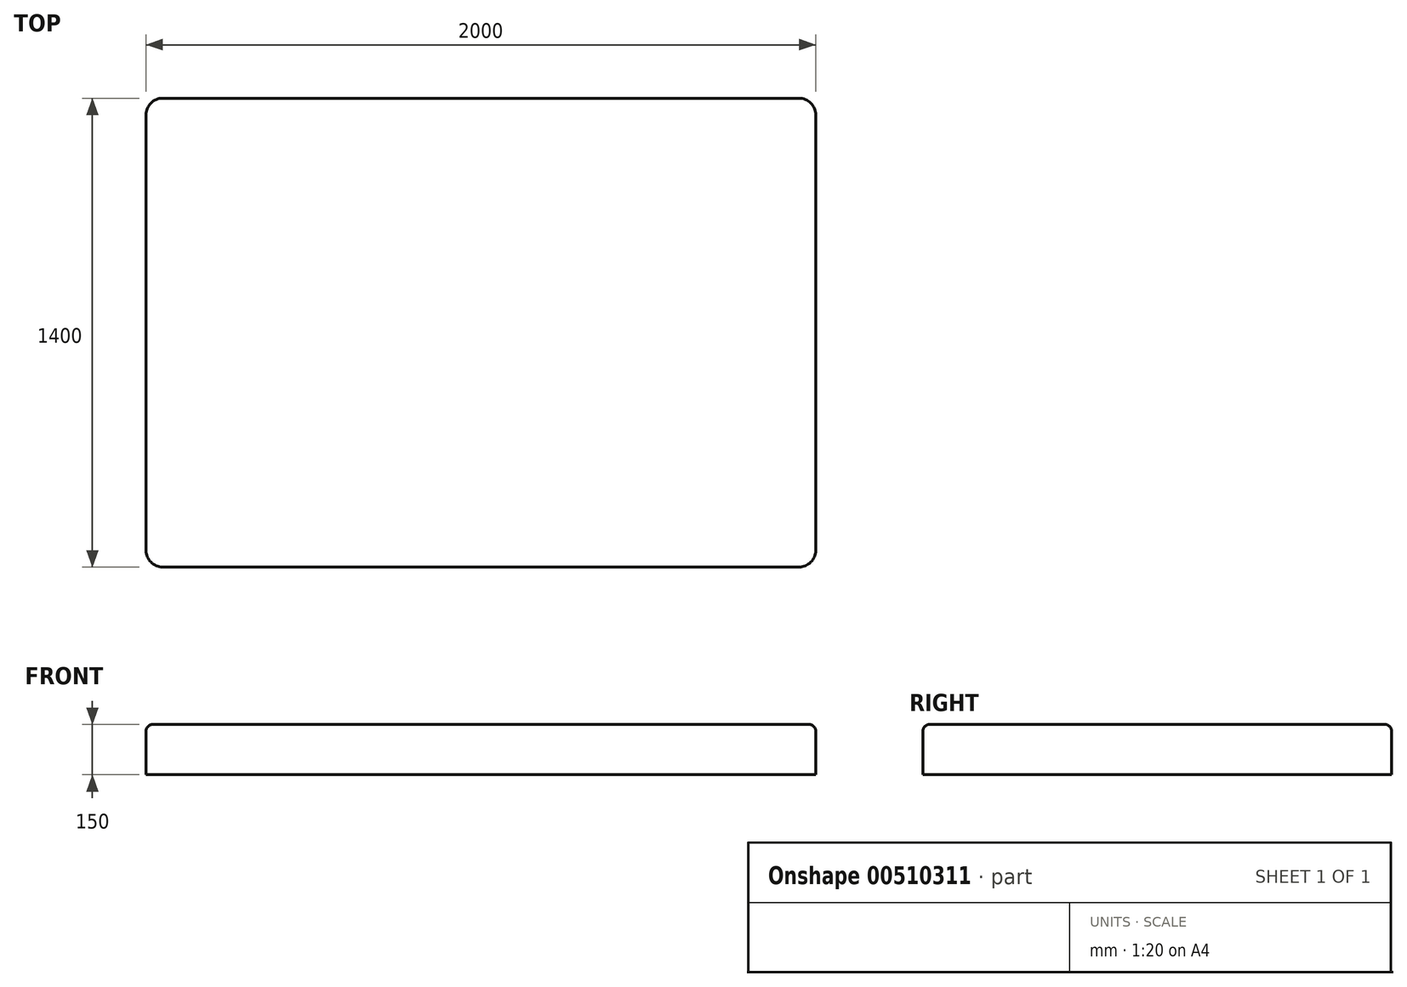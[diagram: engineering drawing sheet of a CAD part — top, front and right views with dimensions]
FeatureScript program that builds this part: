
annotation { "Feature Type Name" : "Feature", "Feature Type Description" : "" }
export const myFeature = defineFeature(function(context is Context, id is Id, definition is map)
    precondition{}
    {
        {
            var Q0;
            Q0=qCreatedBy(makeId("Top.planeOp"),FACE);
            var sketch = newSketch(context, id + "F0", { "sketchPlane" : qUnion([Q0])});
            skLineSegment(sketch, "E0.bottom", {"start": v(-950, 700) * mm, "end": v(950, 700) * mm});
            skLineSegment(sketch, "E0.top", {"start": v(-950, -700) * mm, "end": v(950, -700) * mm});
            skLineSegment(sketch, "E0.left", {"start": v(-1000, 650) * mm, "end": v(-1000, -650) * mm});
            skLineSegment(sketch, "E0.right", {"start": v(1000, 650) * mm, "end": v(1000, -650) * mm});
            skPoint(sketch, "E0.middle", {"position": v(0, 0) * mm});
            skPoint(sketch, "E1.visualSharp", {"position": v(-1000, 700) * mm});
            skArc(sketch, "E1.filletArc", {"start": v(-950, 700) * mm, "mid": v(-985.36, 685.36) * mm, "end": v(-1000, 650) * mm});
            skPoint(sketch, "E2.visualSharp", {"position": v(1000, 700) * mm});
            skArc(sketch, "E2.filletArc", {"start": v(1000, 650) * mm, "mid": v(985.36, 685.36) * mm, "end": v(950, 700) * mm});
            skPoint(sketch, "E3.visualSharp", {"position": v(1000, -700) * mm});
            skArc(sketch, "E3.filletArc", {"start": v(950, -700) * mm, "mid": v(985.36, -685.36) * mm, "end": v(1000, -650) * mm});
            skPoint(sketch, "E4.visualSharp", {"position": v(-1000, -700) * mm});
            skArc(sketch, "E4.filletArc", {"start": v(-1000, -650) * mm, "mid": v(-985.36, -685.36) * mm, "end": v(-950, -700) * mm});
            skSolve(sketch);
        }
        {
            var Q0;
            Q0=makeQuery(id+"F0.imprint","IMPRINT",FACE,{"disambiguationData":[TD([[makeQuery(id+"F0.imprint","IMPRINT",EDGE,{"derivedFrom":sQuery(id+"F0.wireOp",EDGE,"E0.bottom")}),-1.0]])]});
            extrude(context, id + "F1", {"entities" : qUnion([Q0]), "depth" : 150 * mm});
        }
        {
            var Q0;
            Q0=makeQuery(id+"F1.opExtrude","CAP_EDGE",EDGE,{"disambiguationData":[OSD([sQuery(id+"F0.wireOp",EDGE,"E0.top")])],"isStart":false});
            var Q1;
            Q1=makeQuery(id+"F1.opExtrude","CAP_EDGE",EDGE,{"disambiguationData":[OSD([sQuery(id+"F0.wireOp",EDGE,"E4.filletArc")])],"isStart":false});
            var Q2;
            Q2=makeQuery(id+"F1.opExtrude","CAP_EDGE",EDGE,{"disambiguationData":[OSD([sQuery(id+"F0.wireOp",EDGE,"E0.left")])],"isStart":false});
            var Q3;
            Q3=makeQuery(id+"F1.opExtrude","CAP_EDGE",EDGE,{"disambiguationData":[OSD([sQuery(id+"F0.wireOp",EDGE,"E0.bottom")])],"isStart":false});
            var Q4;
            Q4=makeQuery(id+"F1.opExtrude","CAP_EDGE",EDGE,{"disambiguationData":[OSD([sQuery(id+"F0.wireOp",EDGE,"E2.filletArc")])],"isStart":false});
            var Q5;
            Q5=makeQuery(id+"F1.opExtrude","CAP_EDGE",EDGE,{"disambiguationData":[OSD([sQuery(id+"F0.wireOp",EDGE,"E3.filletArc")])],"isStart":false});
            var Q6;
            Q6=makeQuery(id+"F1.opExtrude","CAP_EDGE",EDGE,{"disambiguationData":[OSD([sQuery(id+"F0.wireOp",EDGE,"E0.right")])],"isStart":false});
            fillet(context, id + "F2", {"entities" : qUnion([Q0, Q1, Q2, Q3, Q4, Q5, Q6]), "radius" : 20 * mm, "tangentPropagation" : true, "allowEdgeOverflow" : false});
        }
    });
